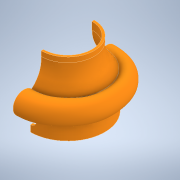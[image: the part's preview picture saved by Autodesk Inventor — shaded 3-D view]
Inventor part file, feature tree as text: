
AUTODESK INVENTOR PART (.ipt)
format: ipt  version: 2022 (Build 260153000, 153)  size: 747,008 bytes
history: native  units: mm
features: sketch x18, extrude x10, plane x4, revolve x3, loft x1, fillet x1
ambient origin geometry x8: Origin, YZ Plane, XZ Plane, XY Plane, X Axis, Y Axis, Z Axis, Center Point
bodies: Solid1 (feature_tree)
feature tree (37):
  sketch  "Sketch1"  dims[d0=65.0mm d1=41.0mm]
  sketch  "Sketch2"  dims[d2=20.5mm d3=0.0mm d4=20.5mm d5=3.5mm d10=3.0mm]
  revolve  "Revolution1"  [1 undecoded]
  sketch  "Sketch5"  dims[d19=7.0mm d22=20.0mm]
  plane  "Work Plane2"
  sketch  "Sketch8"  dims[d23=6.5mm d27=14.5mm]
  plane  "Work Plane4"
  plane  "Work Plane6"
  sketch  "Sketch12"  dims[d30=18.188mm d31=1.5mm]
  loft  "Loft2"
  extrude  "Extrusion2"  TaperAngle=0.0deg  [1 undecoded]
  revolve  "Revolution3"  [1 undecoded]
  revolve  "Revolution4"  [1 undecoded]
  sketch  "Sketch21"  dims[d46=4.5mm d47=3.5mm]
  extrude  "Extrusion4"  Depth=0.5mm
  extrude  "Extrusion5"  Depth=1.5mm
  sketch  "Sketch22"  dims[d48=3.0mm d49=-4.75mm]
  plane  "Work Plane8"
  extrude  "Extrusion6"  Depth=0.5mm
  fillet  "Fillet1"  Radius=7.6mm
  extrude  "Extrusion7"  Depth=5.0mm
  extrude  "Extrusion8"  Depth=3.5mm
  extrude  "Extrusion10"  [1 undecoded]
  extrude  "Extrusion11"  Depth=24.0mm
  extrude  "Extrusion12"  Depth=12.5mm
  extrude  "Extrusion14"  TaperAngle=0.0deg  [1 undecoded]
  sketch  "Sketch3"  dims[d11=2.6mm d13=0.0mm]
  sketch  "Sketch9"  dims[d28=14.0mm d29=0.5mm]
  sketch  "Sketch17"  dims[d33=1.0mm d34=0.5mm d35=7.6mm]
  sketch  "Sketch18"  dims[d36=360.0deg d45=5.0mm]
  sketch  "Sketch23"  dims[d50=27.0mm d51=24.0mm]
  sketch  "Sketch24"  dims[d65=15.0mm d66=12.5mm]
  sketch  "Sketch25"  dims[d67=0.0mm d68=90.0deg d69=0.0mm d70=90.0deg]
  sketch  "Sketch29"  dims[d71=0.0mm d72=90.0deg]
  sketch  "Sketch30"  dims[d80=12.5mm]
  sketch  "Sketch31"  dims[d81=15.0mm]
  sketch  "Sketch33"  dims[d82=28.8mm d83=0.0mm d84=360.0deg d85=22.0mm d86=90.0deg d89=2.5mm d90=0.0mm d91=10.0mm d92=0.0mm d93=5.0mm d94=0.0mm d95=0.1mm d96=42.0mm d97=2.0mm d98=0.0mm d99=0.2mm d103=0.2mm d104=42.0mm d105=45.0mm d106=13.0mm d107=0.0mm d119=10.0mm d120=0.0mm d121=3.0mm d122=0.0mm d123=7.0mm d124=7.05mm d125=0.0mm d126=0.0mm d129=0.0mm d130=0.0mm]
note: 6 required parameter values undecoded (feature->parameter linkage not recoverable at this tier; creation-order binding heuristic only, values carry confidence <= 0.55)